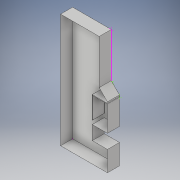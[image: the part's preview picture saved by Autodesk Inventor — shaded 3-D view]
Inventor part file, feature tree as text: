
AUTODESK INVENTOR PART (.ipt)
format: ipt  version: 2017 (Build 210142000, 142)  size: 147,456 bytes
history: native  units: in
note: dims shown in document units (in); Inventor stores cm internally (conversion verified against a paired STEP export)
features: sketch x4, extrude x3, plane x1, chamfer x1, shell x1
ambient origin geometry x8: Origin, YZ Plane, XZ Plane, XY Plane, X Axis, Y Axis, Z Axis, Center Point
bodies: Body1 (feature_tree)
feature tree (10):
  sketch  "Sketch1"  dims[d0=1080.0in d1=300.0in d5=114.0in d6=0.0in]
  plane  "Work Plane1"
  sketch  "Sketch2"  dims[d7=78.0in d8=0.125in d9=45.0deg d10=114.0in d11=0.0in d12=0.1in]
  extrude  "Extrusion2"  Depth=300.0in
  chamfer  "Chamfer1"  Distance=114.0in
  extrude  "Extrusion3"  Depth=114.0in TaperAngle=0.0deg
  shell  "Shell2"  Thickness=0.1in
  extrude  "Extrusion4"  Depth=114.0in TaperAngle=0.0deg
  sketch  "Sketch3"  dims[d13=1.0in d14=114.0in d15=0.0in]
  sketch  "Sketch4"
